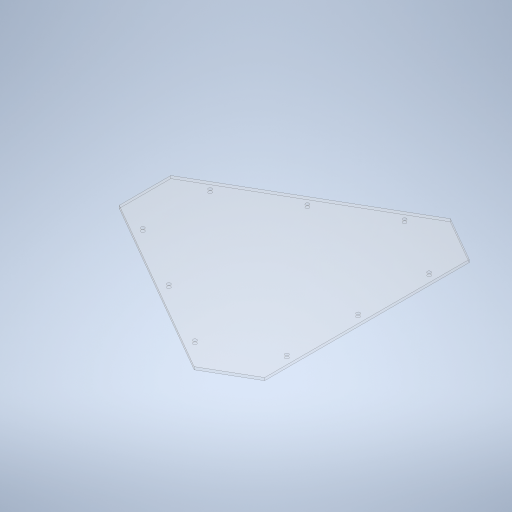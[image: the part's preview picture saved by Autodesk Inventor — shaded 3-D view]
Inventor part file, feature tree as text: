
AUTODESK INVENTOR PART (.ipt)
format: ipt  version: 2024.2 (Build 282272000, 272)  size: 276,992 bytes
history: native  units: mm
features: sketch x3, hole x2, extrude x1
ambient origin geometry x8: Origin, YZ Plane, XZ Plane, XY Plane, X Axis, Y Axis, Z Axis, Center Point
bodies: Solid1 (feature_tree)
feature tree (6):
  extrude  "Extrusion1"  TaperAngle=60.0deg  [1 undecoded]
  hole  "Hole1"  [1 undecoded]
  hole  "Hole2"  [1 undecoded]
  sketch  "Sketch1"  dims[d0=60.0deg d1=60.0deg]
  sketch  "Sketch2"  dims[d3=58.0mm d5=60.0deg]
  sketch  "Sketch3"  dims[d6=60.0deg d7=58.0mm d8=58.0mm d9=3.0mm d10=0.0mm d11=10.0mm d12=80.0mm d13=80.0mm d14=10.0mm d15=10.0mm d16=4.0mm d17=6.0mm d18=4.0mm d19=2.0mm d20=90.0deg d21=8.0mm d22=20.594885mm d23=160.0mm d24=160.0mm d25=10.0mm d26=10.0mm d27=4.0mm d28=6.0mm d29=4.0mm d30=2.0mm d31=90.0deg d32=8.0mm d33=20.594885mm d34=230.0mm]
note: 3 required parameter values undecoded (feature->parameter linkage not recoverable at this tier; creation-order binding heuristic only, values carry confidence <= 0.55)
